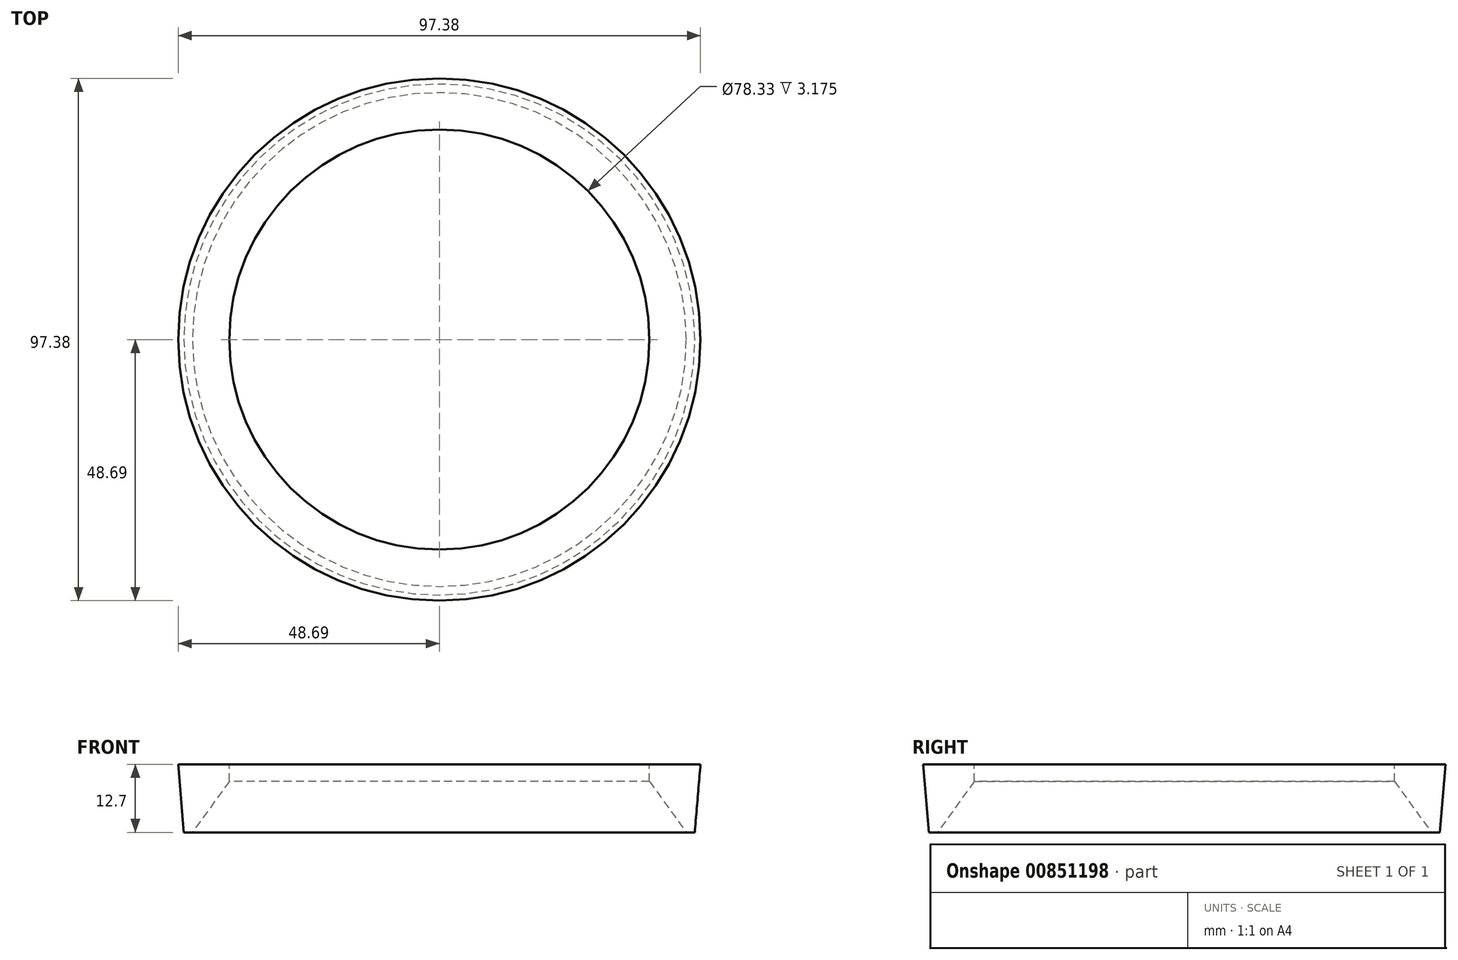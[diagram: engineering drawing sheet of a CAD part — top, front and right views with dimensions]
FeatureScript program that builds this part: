
annotation { "Feature Type Name" : "Feature", "Feature Type Description" : "" }
export const myFeature = defineFeature(function(context is Context, id is Id, definition is map)
    precondition{}
    {
        {
            var Q0;
            Q0=qCreatedBy(makeId("Front.planeOp"),FACE);
            var sketch = newSketch(context, id + "F0", { "sketchPlane" : qUnion([Q0])});
            skLineSegment(sketch, "E0", {"start": v(39.17, 0) * mm, "end": v(39.17, -3.18) * mm});
            skLineSegment(sketch, "E1", {"start": v(39.17, -3.18) * mm, "end": v(46.04, -12.7) * mm});
            skLineSegment(sketch, "E2", {"start": v(46.04, -12.7) * mm, "end": v(47.63, -12.7) * mm});
            skLineSegment(sketch, "E3", {"start": v(47.63, -12.7) * mm, "end": v(48.7, 0) * mm});
            skLineSegment(sketch, "E4", {"start": v(48.7, 0) * mm, "end": v(44.36, 0) * mm});
            skLineSegment(sketch, "E5", {"start": v(39.17, 0) * mm, "end": v(41.37, 0) * mm});
            skArc(sketch, "E6", {"start": v(41.37, 0) * mm, "mid": v(42.86, -1.06) * mm, "end": v(44.36, 0) * mm});
            skLineSegment(sketch, "E7", {"start": v(40.45, -1.06) * mm, "end": v(46, -1.06) * mm, "construction": true});
            skLineSegment(sketch, "E8", {"start": v(0, 15.42) * mm, "end": v(0, -20.5) * mm, "construction": true});
            skLineSegment(sketch, "E9", {"start": v(41.37, 0) * mm, "end": v(44.36, 0) * mm});
            skSolve(sketch);
        }
        {
            var Q0;
            Q0=qSketchRegion(id+"F0",true);
            var Q1;
            Q1=sQuery(id+"F0.wireOp",EDGE,"E8");
            revolve(context, id + "F1", {"surfaceOperationType" : NewSurfaceOperationType.NEW, "entities" : qUnion([Q0]), "axis" : qUnion([Q1]), "revolveType" : RevolveType.FULL});
        }
    });
